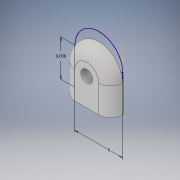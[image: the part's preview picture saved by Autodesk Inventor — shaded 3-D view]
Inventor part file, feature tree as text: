
AUTODESK INVENTOR PART (.ipt)
format: ipt  version: 2019 (Build 230136000, 136)  size: 123,904 bytes
history: native  units: mm
features: other x1, sketch x1, extrude x1, hole x1, fillet x1
ambient origin geometry x8: Origin, YZ Plane, XZ Plane, XY Plane, X Axis, Y Axis, Z Axis, Center Point
bodies: Body1 (feature_tree)
feature tree (5):
  other  "Bryła1"
  sketch  "Szkic1"
  extrude  "Wyciągnięcie proste1"  Depth=8.0mm
  hole  "Otwór1"  [1 undecoded]
  fillet  "Zaokrąglenie1"  Radius=2.0mm
note: 1 required parameter value undecoded (feature->parameter linkage not recoverable at this tier; creation-order binding heuristic only, values carry confidence <= 0.55)
